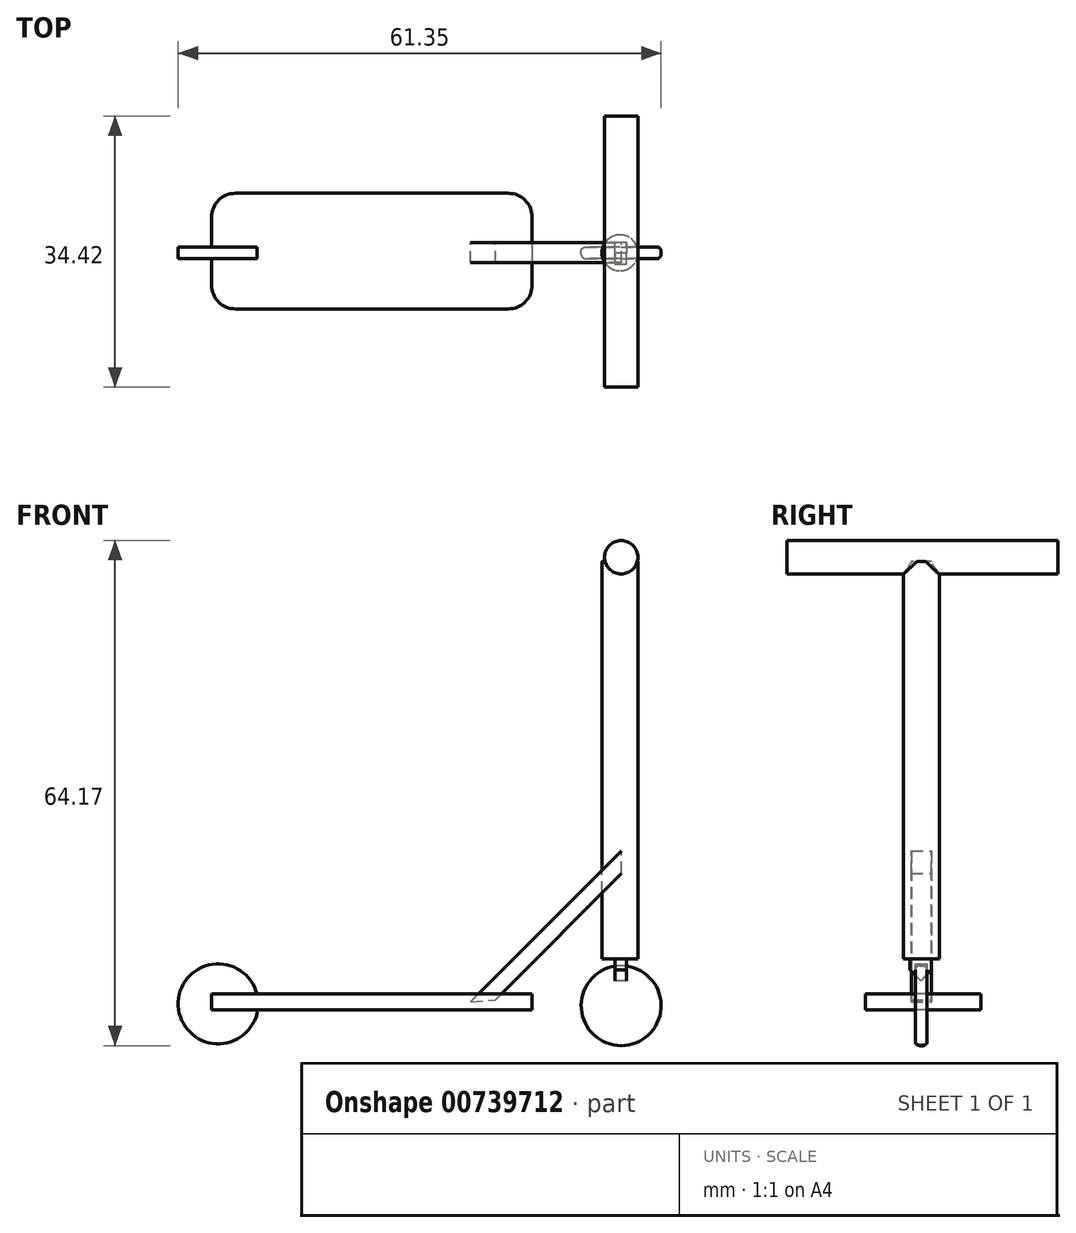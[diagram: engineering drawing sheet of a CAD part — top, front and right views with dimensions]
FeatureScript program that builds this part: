
annotation { "Feature Type Name" : "Feature", "Feature Type Description" : "" }
export const myFeature = defineFeature(function(context is Context, id is Id, definition is map)
    precondition{}
    {
        {
            var Q0;
            Q0=qCreatedBy(makeId("Right.planeOp"),FACE);
            cPlane(context, id + "F0", {"entities" : qUnion([Q0]), "cplaneType" : CPlaneType.OFFSET, "offset" : 48.5 * mm, "width" : 152.4 * mm, "height" : 152.4 * mm});
        }
        {
            var Q0;
            Q0=qCreatedBy(id+"F0.planeOp",FACE);
            var sketch = newSketch(context, id + "F1", { "sketchPlane" : qUnion([Q0])});
            skLineSegment(sketch, "E0", {"start": v(0, 0) * mm, "end": v(0, 56.96) * mm});
            skSolve(sketch);
        }
        {
            var Q0;
            Q0=qCreatedBy(makeId("Top.planeOp"),FACE);
            var sketch = newSketch(context, id + "F2", { "sketchPlane" : qUnion([Q0])});
            skCircle(sketch, "E1", {"center": v(43.62, 0) * mm, "radius": 2.29 * mm});
            skSolve(sketch);
        }
        {
            var Q0;
            Q0=makeQuery(id+"F2.imprint","IMPRINT",FACE,{"disambiguationData":[TD([[makeQuery(id+"F2.imprint","IMPRINT",EDGE,{"derivedFrom":sQuery(id+"F2.wireOp",EDGE,"E1")}),1.0]])]});
            var Q1;
            Q1=sQuery(id+"F1.wireOp",EDGE,"E0");
            sweep(context, id + "F3", {"profiles" : qUnion([Q0]), "path" : qUnion([Q1])});
        }
        {
            var Q0;
            Q0=qCreatedBy(id+"F0.planeOp",FACE);
            cPlane(context, id + "F4", {"entities" : qUnion([Q0]), "cplaneType" : CPlaneType.OFFSET, "offset" : 4.7 * mm, "oppositeDirection" : true, "width" : 152.4 * mm, "height" : 152.4 * mm});
        }
        {
            var Q0;
            Q0=qCreatedBy(id+"F4.planeOp",FACE);
            var sketch = newSketch(context, id + "F5", { "sketchPlane" : qUnion([Q0])});
            skLineSegment(sketch, "E2", {"start": v(-17.05, 57.51) * mm, "end": v(17.37, 57.51) * mm});
            skSolve(sketch);
        }
        {
            var Q0;
            Q0=qCreatedBy(makeId("Top.planeOp"),FACE);
            var sketch = newSketch(context, id + "F6", { "sketchPlane" : qUnion([Q0])});
            skLineSegment(sketch, "E3.bottom", {"start": v(32.47, 7.57) * mm, "end": v(-8.26, 7.57) * mm});
            skLineSegment(sketch, "E3.top", {"start": v(32.47, -7.13) * mm, "end": v(-8.26, -7.13) * mm});
            skLineSegment(sketch, "E3.left", {"start": v(32.47, 7.57) * mm, "end": v(32.47, -7.13) * mm});
            skLineSegment(sketch, "E3.right", {"start": v(-8.26, 7.57) * mm, "end": v(-8.26, -7.13) * mm});
            skSolve(sketch);
        }
        {
            var Q0;
            Q0 = qSketchRegion(id + "F6", true);
            extrude(context, id + "F7", {"entities" : qUnion([Q0]), "depth" : 2.03 * mm, "offsetDistance" : 25.4 * mm});
        }
        {
            var Q0;
            Q0=makeQuery(id+"F7.opExtrude","SWEPT_EDGE",EDGE,{"disambiguationData":[OSD([sQuery(id+"F6.wireOp",EDGE,"E3.top"),sQuery(id+"F6.wireOp",EDGE,"E3.right")])]});
            var Q1;
            Q1=makeQuery(id+"F7.opExtrude","SWEPT_EDGE",EDGE,{"disambiguationData":[OSD([sQuery(id+"F6.wireOp",EDGE,"E3.bottom"),sQuery(id+"F6.wireOp",EDGE,"E3.right")])]});
            var Q2;
            Q2=makeQuery(id+"F7.opExtrude","SWEPT_EDGE",EDGE,{"disambiguationData":[OSD([sQuery(id+"F6.wireOp",EDGE,"E3.top"),sQuery(id+"F6.wireOp",EDGE,"E3.left")])]});
            var Q3;
            Q3=makeQuery(id+"F7.opExtrude","SWEPT_EDGE",EDGE,{"disambiguationData":[OSD([sQuery(id+"F6.wireOp",EDGE,"E3.bottom"),sQuery(id+"F6.wireOp",EDGE,"E3.left")])]});
            fillet(context, id + "F8", {"entities" : qUnion([Q0, Q1, Q2, Q3]), "radius" : 3.05 * mm, "tangentPropagation" : true, "allowEdgeOverflow" : false});
        }
        {
            var Q0;
            Q0=qCreatedBy(makeId("Front.planeOp"),FACE);
            var sketch = newSketch(context, id + "F9", { "sketchPlane" : qUnion([Q0])});
            skLineSegment(sketch, "E4", {"start": v(27.81, 1.25) * mm, "end": v(43.8, 17.34) * mm});
            skLineSegment(sketch, "E5", {"start": v(43.8, 17.34) * mm, "end": v(43.8, 20.2) * mm});
            skLineSegment(sketch, "E6", {"start": v(43.8, 20.2) * mm, "end": v(24.66, 1.05) * mm});
            skLineSegment(sketch, "E7", {"start": v(24.66, 1.05) * mm, "end": v(27.81, 1.25) * mm});
            skSolve(sketch);
        }
        {
            var Q0;
            Q0 = qSketchRegion(id + "F9", true);
            extrude(context, id + "F10", {"entities" : qUnion([Q0]), "endBound" : BoundingType.SYMMETRIC, "depth" : 2.54 * mm, "offsetDistance" : 25.4 * mm});
        }
        {
            var Q0;
            Q0=qCreatedBy(makeId("Front.planeOp"),FACE);
            var sketch = newSketch(context, id + "F11", { "sketchPlane" : qUnion([Q0])});
            skCircle(sketch, "E8", {"center": v(43.77, 0.54) * mm, "radius": 5.08 * mm});
            skCircle(sketch, "E9", {"center": v(-7.42, 0.77) * mm, "radius": 5.08 * mm});
            skSolve(sketch);
        }
        {
            var Q0;
            Q0=qCreatedBy(makeId("Top.planeOp"),FACE);
            var sketch = newSketch(context, id + "F12", { "sketchPlane" : qUnion([Q0])});
            skCircle(sketch, "E10", {"center": v(43.67, 0) * mm, "radius": 2.65 * mm});
            skSolve(sketch);
        }
        {
            var Q0;
            Q0 = qSketchRegion(id + "F12", true);
            extrude(context, id + "F13", {"entities" : qUnion([Q0]), "operationType" : NewBodyOperationType.REMOVE, "depth" : 6.48 * mm, "offsetDistance" : 25.4 * mm});
        }
        {
            var Q0;
            Q0 = qSketchRegion(id + "F11", true);
            extrude(context, id + "F14", {"entities" : qUnion([Q0]), "operationType" : NewBodyOperationType.ADD, "endBound" : BoundingType.SYMMETRIC, "depth" : 1.47 * mm, "offsetDistance" : 25.4 * mm});
        }
        {
            var Q0;
            Q0=makeQuery(id+"F14.opExtrude","CAP_FACE",FACE,{"disambiguationData":[OSD([sQuery(id+"F11.wireOp",EDGE,"E9")])],"isStart":false});
            var Q1;
            Q1=makeQuery(id+"F14.opExtrude","CAP_FACE",FACE,{"disambiguationData":[OSD([sQuery(id+"F11.wireOp",EDGE,"E8")])],"isStart":false});
            var Q2;
            Q2=makeQuery(id+"F14.opExtrude","CAP_FACE",FACE,{"disambiguationData":[OSD([sQuery(id+"F11.wireOp",EDGE,"E8")])],"isStart":true});
            var Q3;
            Q3=makeQuery(id+"F14.opExtrude","CAP_EDGE",EDGE,{"disambiguationData":[OSD([sQuery(id+"F11.wireOp",EDGE,"E9")])],"isStart":true});
            fillet(context, id + "F15", {"entities" : qUnion([Q0, Q1, Q2, Q3]), "radius" : 0.55 * mm, "tangentPropagation" : true, "allowEdgeOverflow" : false});
        }
        {
            var Q0;
            Q0=makeQuery(id+"F13.boolean.opBoolean","COPY",FACE,{"derivedFrom":makeQuery(id+"F13.opExtrude","CAP_FACE",FACE,{"disambiguationData":[OSD([sQuery(id+"F12.wireOp",EDGE,"E10")])],"isStart":false})});
            var sketch = newSketch(context, id + "F16", { "sketchPlane" : qUnion([Q0])});
            skLineSegment(sketch, "E11.bottom", {"start": v(44.46, 1.42) * mm, "end": v(42.98, 1.42) * mm});
            skLineSegment(sketch, "E11.top", {"start": v(44.46, -1.32) * mm, "end": v(42.98, -1.32) * mm});
            skLineSegment(sketch, "E11.left", {"start": v(44.46, 1.42) * mm, "end": v(44.46, -1.32) * mm});
            skLineSegment(sketch, "E11.right", {"start": v(42.98, 1.42) * mm, "end": v(42.98, -1.32) * mm});
            skSolve(sketch);
        }
        {
            var Q0;
            Q0 = qSketchRegion(id + "F16", true);
            extrude(context, id + "F17", {"entities" : qUnion([Q0]), "depth" : 3.43 * mm, "offsetDistance" : 25.4 * mm});
        }
        {
            var Q0;
            Q0=makeQuery(id+"F17.opExtrude","CAP_EDGE",EDGE,{"disambiguationData":[OSD([sQuery(id+"F16.wireOp",EDGE,"E11.bottom")])],"isStart":false});
            var Q1;
            Q1=makeQuery(id+"F17.opExtrude","CAP_EDGE",EDGE,{"disambiguationData":[OSD([sQuery(id+"F16.wireOp",EDGE,"E11.top")])],"isStart":false});
            chamfer(context, id + "F18", {"entities" : qUnion([Q0, Q1]), "width" : 2.03 * mm, "tangentPropagation" : true});
        }
        {
            var Q0;
            Q0=qCreatedBy(makeId("Front.planeOp"),FACE);
            cPlane(context, id + "F19", {"entities" : qUnion([Q0]), "cplaneType" : CPlaneType.OFFSET, "offset" : 11.43 * mm, "width" : 152.4 * mm, "height" : 152.4 * mm});
        }
        {
            var Q0;
            Q0=qCreatedBy(id+"F19.planeOp",FACE);
            var sketch = newSketch(context, id + "F20", { "sketchPlane" : qUnion([Q0])});
            skCircle(sketch, "E12", {"center": v(43.78, 57.5) * mm, "radius": 2.12 * mm});
            skSolve(sketch);
        }
        {
            var Q0;
            Q0=makeQuery(id+"F20.imprint","IMPRINT",FACE,{"disambiguationData":[TD([[makeQuery(id+"F20.imprint","IMPRINT",EDGE,{"derivedFrom":sQuery(id+"F20.wireOp",EDGE,"E12")}),1.0]])]});
            var Q1;
            Q1=sQuery(id+"F5.wireOp",EDGE,"E2");
            sweep(context, id + "F21", {"operationType" : NewBodyOperationType.ADD, "profiles" : qUnion([Q0]), "path" : qUnion([Q1])});
        }
    });
